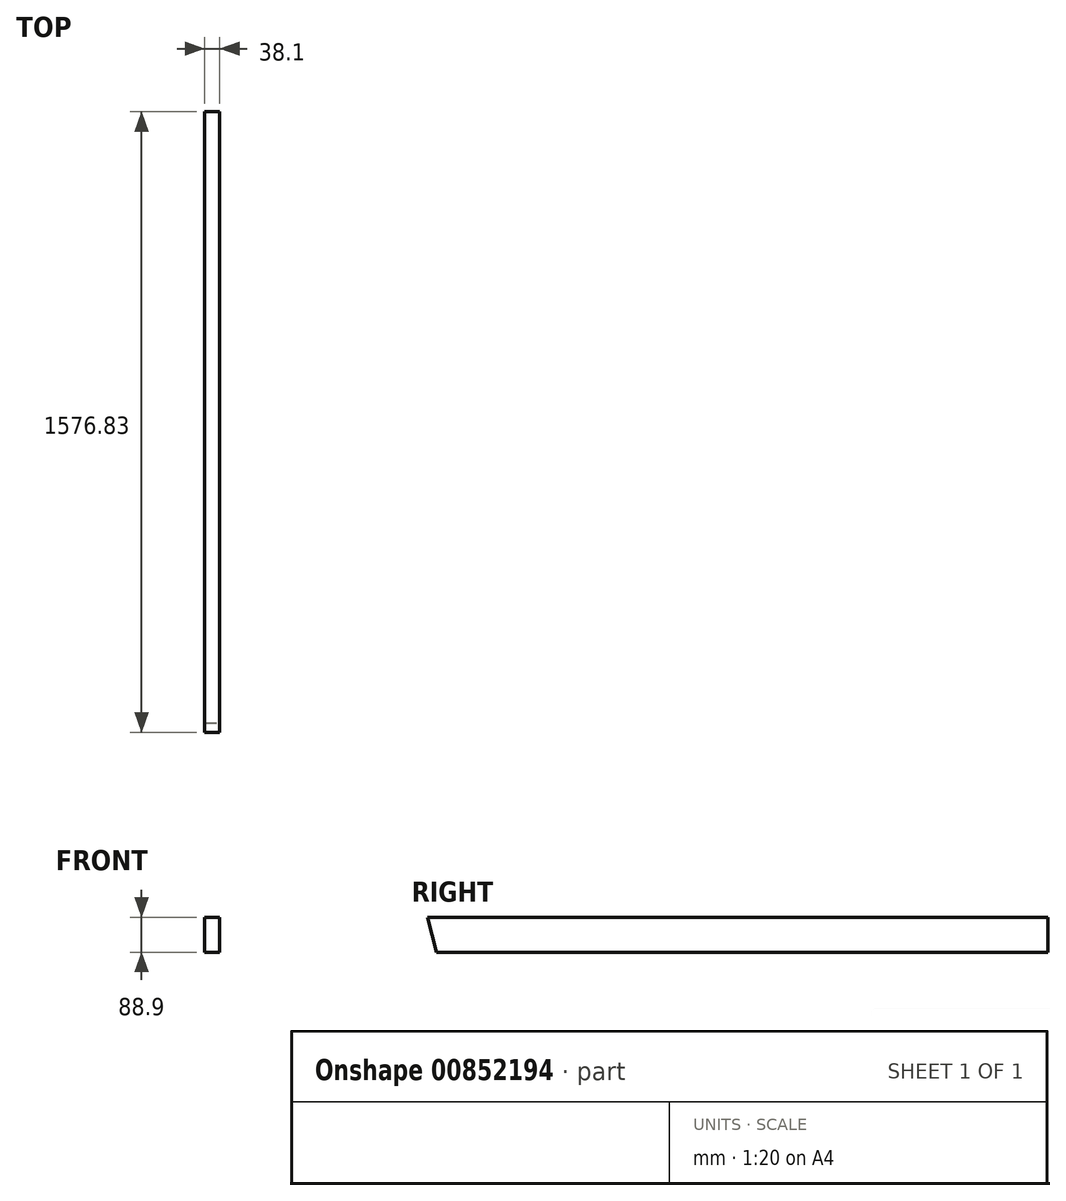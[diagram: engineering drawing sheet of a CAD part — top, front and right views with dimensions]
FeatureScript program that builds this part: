
annotation { "Feature Type Name" : "Feature", "Feature Type Description" : "" }
export const myFeature = defineFeature(function(context is Context, id is Id, definition is map)
    precondition{}
    {
        {
            var Q0;
            Q0=qCreatedBy(makeId("Front.planeOp"),FACE);
            var sketch = newSketch(context, id + "F0", { "sketchPlane" : qUnion([Q0])});
            skLineSegment(sketch, "E0.bottom", {"start": v(19.05, -44.45) * mm, "end": v(-19.05, -44.45) * mm});
            skLineSegment(sketch, "E0.top", {"start": v(19.05, 44.45) * mm, "end": v(-19.05, 44.45) * mm});
            skLineSegment(sketch, "E0.left", {"start": v(19.05, -44.45) * mm, "end": v(19.05, 44.45) * mm});
            skLineSegment(sketch, "E0.right", {"start": v(-19.05, -44.45) * mm, "end": v(-19.05, 44.45) * mm});
            skPoint(sketch, "E0.middle", {"position": v(0, 0) * mm});
            skSolve(sketch);
        }
        {
            var Q0;
            Q0=makeQuery(id+"F0.imprint","IMPRINT",FACE,{"disambiguationData":[TD([[makeQuery(id+"F0.imprint","IMPRINT",EDGE,{"derivedFrom":sQuery(id+"F0.wireOp",EDGE,"E0.bottom")}),-1.0]])]});
            extrude(context, id + "F1", {"entities" : qUnion([Q0]), "depth" : 1576.83 * mm, "offsetDistance" : 25.4 * mm});
        }
        {
            var Q0;
            Q0=qCreatedBy(makeId("Right.planeOp"),FACE);
            var sketch = newSketch(context, id + "F2", { "sketchPlane" : qUnion([Q0])});
            skLineSegment(sketch, "E1", {"start": v(-1576.83, 44.45) * mm, "end": v(-1552.96, -44.45) * mm});
            skLineSegment(sketch, "E2", {"start": v(-1552.96, -44.45) * mm, "end": v(-1576.83, -44.45) * mm});
            skLineSegment(sketch, "E3", {"start": v(-1576.83, -44.45) * mm, "end": v(-1576.83, 44.45) * mm});
            skSolve(sketch);
        }
        {
            var Q0;
            Q0=qSketchRegion(id+"F2",true);
            extrude(context, id + "F3", {"entities" : qUnion([Q0]), "operationType" : NewBodyOperationType.REMOVE, "endBound" : BoundingType.SYMMETRIC, "oppositeDirection" : true, "depth" : 50.8 * mm, "offsetDistance" : 25.4 * mm});
        }
    });
